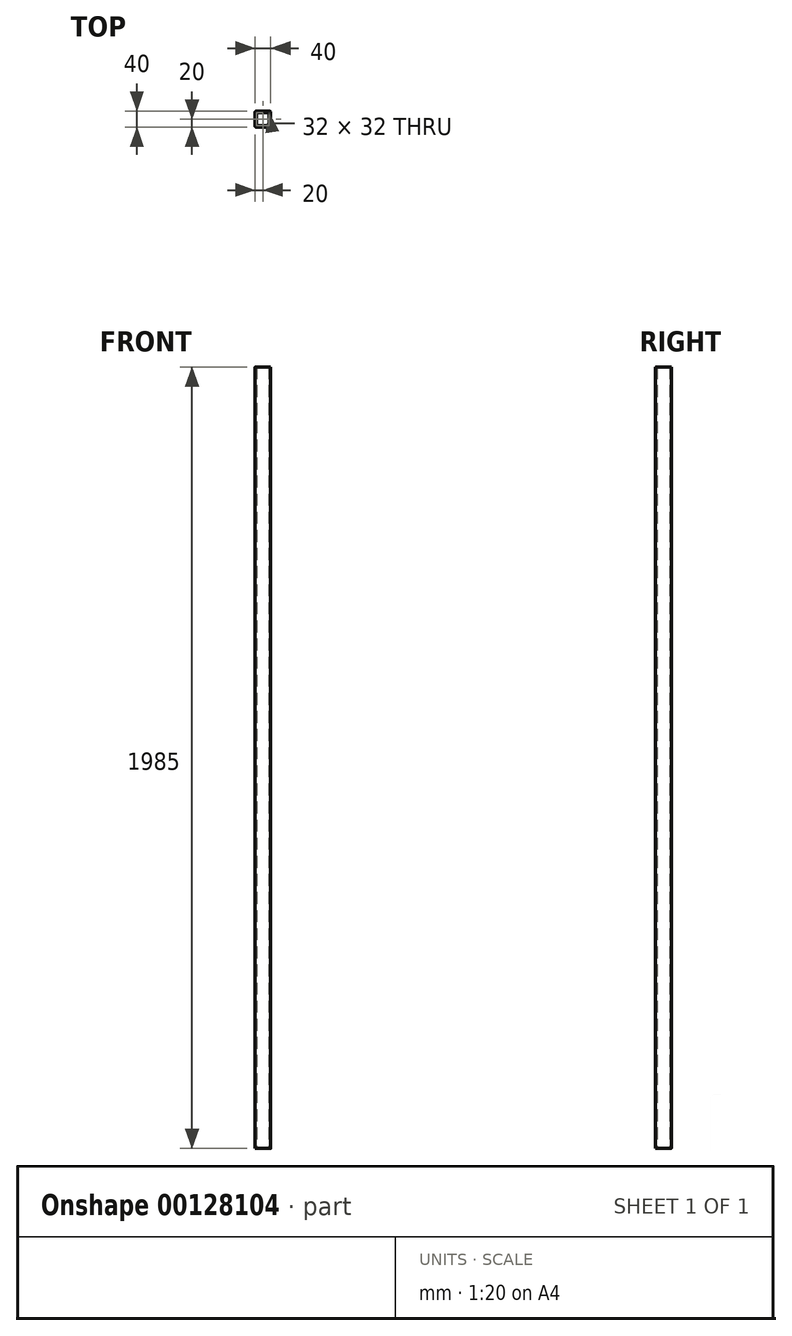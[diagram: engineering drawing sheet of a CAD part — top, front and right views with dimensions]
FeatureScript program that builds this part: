
annotation { "Feature Type Name" : "Feature", "Feature Type Description" : "" }
export const myFeature = defineFeature(function(context is Context, id is Id, definition is map)
    precondition{}
    {
        {
            var Q0;
            Q0=qCreatedBy(makeId("Top.planeOp"),FACE);
            var sketch = newSketch(context, id + "F0", { "sketchPlane" : qUnion([Q0])});
            skLineSegment(sketch, "E0.bottom", {"start": v(2.5, 0) * mm, "end": v(37.5, 0) * mm});
            skLineSegment(sketch, "E0.top", {"start": v(2.5, 40) * mm, "end": v(37.5, 40) * mm});
            skLineSegment(sketch, "E0.left", {"start": v(0, 2.5) * mm, "end": v(0, 37.5) * mm});
            skLineSegment(sketch, "E0.right", {"start": v(40, 2.5) * mm, "end": v(40, 37.5) * mm});
            skPoint(sketch, "E1.visualSharp", {"position": v(0, 40) * mm});
            skArc(sketch, "E1.filletArc", {"start": v(2.5, 40) * mm, "mid": v(0.73, 39.27) * mm, "end": v(0, 37.5) * mm});
            skPoint(sketch, "E2.visualSharp", {"position": v(40, 40) * mm});
            skArc(sketch, "E2.filletArc", {"start": v(40, 37.5) * mm, "mid": v(39.27, 39.27) * mm, "end": v(37.5, 40) * mm});
            skPoint(sketch, "E3.visualSharp", {"position": v(40, 0) * mm});
            skArc(sketch, "E3.filletArc", {"start": v(37.5, 0) * mm, "mid": v(39.27, 0.73) * mm, "end": v(40, 2.5) * mm});
            skPoint(sketch, "E4.visualSharp", {"position": v(0, 0) * mm});
            skArc(sketch, "E4.filletArc", {"start": v(0, 2.5) * mm, "mid": v(0.73, 0.73) * mm, "end": v(2.5, 0) * mm});
            skLineSegment(sketch, "E5.0", {"start": v(36, 4) * mm, "end": v(36, 36) * mm});
            skLineSegment(sketch, "E5.1", {"start": v(4, 4) * mm, "end": v(36, 4) * mm});
            skLineSegment(sketch, "E5.2", {"start": v(4, 4) * mm, "end": v(4, 36) * mm});
            skLineSegment(sketch, "E5.3", {"start": v(4, 36) * mm, "end": v(36, 36) * mm});
            skSolve(sketch);
        }
        {
            var Q0;
            Q0 = qSketchRegion(id + "F0", true);
            extrude(context, id + "F1", {"entities" : qUnion([Q0]), "depth" : (2000 - 15) * mm});
        }
    });
